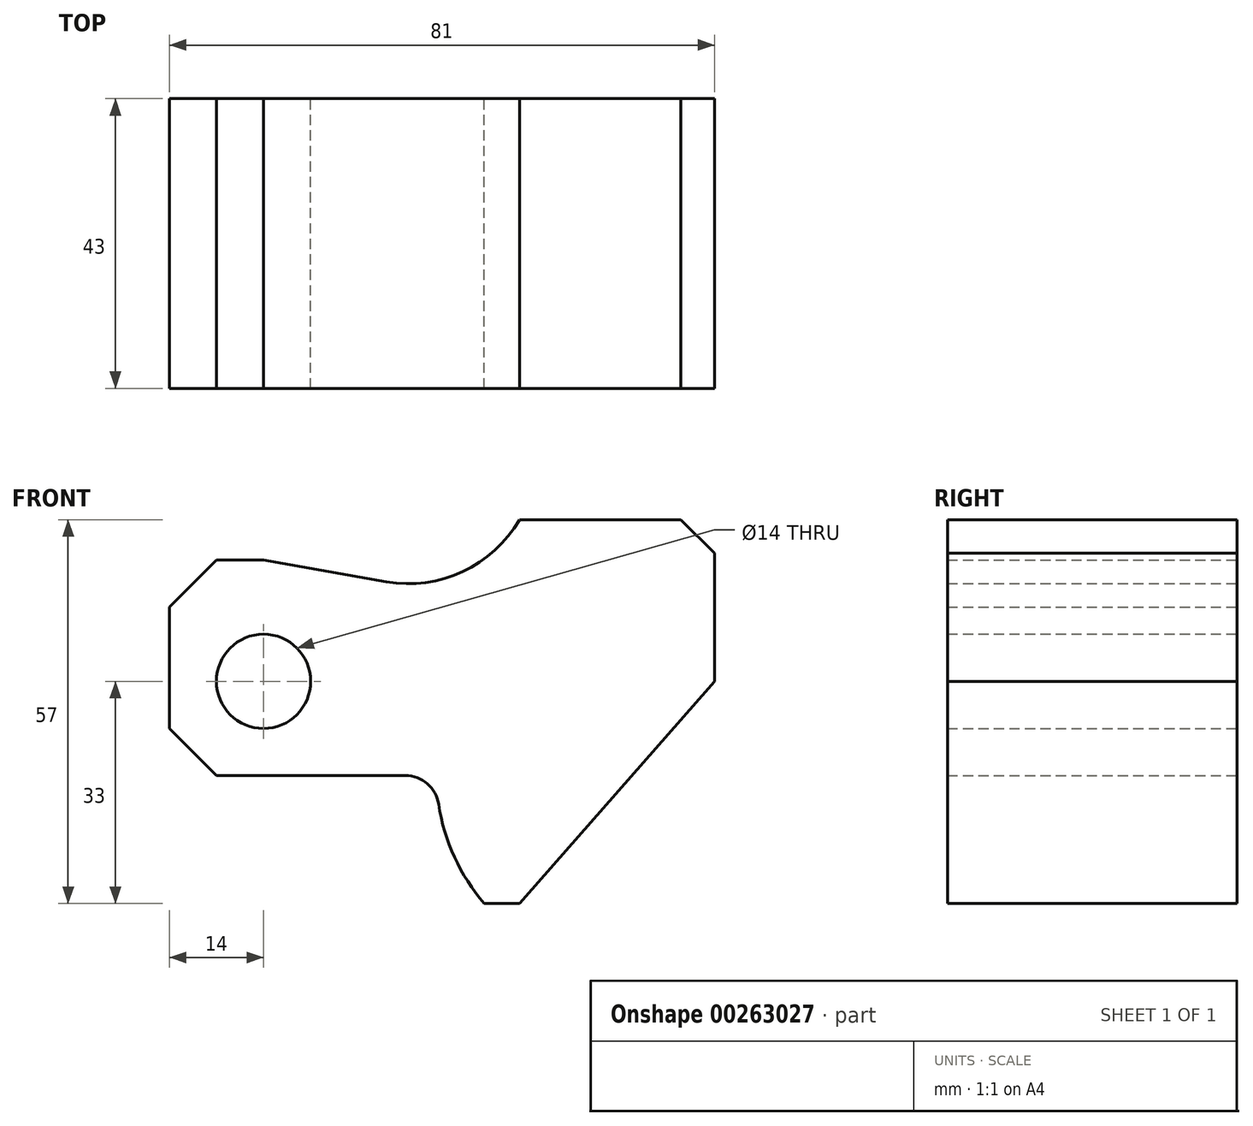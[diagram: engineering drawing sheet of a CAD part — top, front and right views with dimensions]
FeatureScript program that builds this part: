
annotation { "Feature Type Name" : "Feature", "Feature Type Description" : "" }
export const myFeature = defineFeature(function(context is Context, id is Id, definition is map)
    precondition{}
    {
        {
            var Q0;
            Q0=qCreatedBy(makeId("Front.planeOp"),FACE);
            var sketch = newSketch(context, id + "F0", { "sketchPlane" : qUnion([Q0])});
            skCircle(sketch, "E0", {"center": v(0, 0) * mm, "radius": 7 * mm});
            skLineSegment(sketch, "E1", {"start": v(-14, -7) * mm, "end": v(-14, 11) * mm});
            skLineSegment(sketch, "E2", {"start": v(-14, 11) * mm, "end": v(-7, 18) * mm});
            skLineSegment(sketch, "E3", {"start": v(-7, 18) * mm, "end": v(0, 18) * mm});
            skLineSegment(sketch, "E4", {"start": v(0, 18) * mm, "end": v(18.24, 14.78) * mm});
            skArc(sketch, "E5", {"start": v(18.24, 14.78) * mm, "mid": v(29.57, 16.28) * mm, "end": v(38, 24) * mm});
            skLineSegment(sketch, "E6", {"start": v(38, 24) * mm, "end": v(62, 24) * mm});
            skLineSegment(sketch, "E7", {"start": v(21.07, -14) * mm, "end": v(-7, -14) * mm});
            skLineSegment(sketch, "E8", {"start": v(-14, -7) * mm, "end": v(-7, -14) * mm});
            skLineSegment(sketch, "E9", {"start": v(62, 24) * mm, "end": v(67, 19) * mm});
            skLineSegment(sketch, "E10", {"start": v(67, 0) * mm, "end": v(67, 19) * mm});
            skPoint(sketch, "E11", {"position": v(21.07, -14) * mm});
            skPoint(sketch, "E12.start.orphan", {"position": v(38, -33) * mm});
            skArc(sketch, "E13", {"start": v(26.01, -18.26) * mm, "mid": v(24.33, -15.21) * mm, "end": v(21.07, -14) * mm});
            skLineSegment(sketch, "E14", {"start": v(38, -33) * mm, "end": v(67, 0) * mm});
            skLineSegment(sketch, "E15", {"start": v(38, -33) * mm, "end": v(32.79, -33) * mm});
            skArc(sketch, "E16", {"start": v(26.01, -18.26) * mm, "mid": v(28.35, -26.12) * mm, "end": v(32.79, -33) * mm});
            skSolve(sketch);
        }
        {
            var Q0;
            Q0=makeQuery(id+"F0.imprint","IMPRINT",FACE,{"disambiguationData":[TD([[makeQuery(id+"F0.imprint","IMPRINT",EDGE,{"derivedFrom":sQuery(id+"F0.wireOp",EDGE,"E0")}),-1.0]])]});
            extrude(context, id + "F1", {"entities" : qUnion([Q0]), "depth" : 43 * mm});
        }
    });
